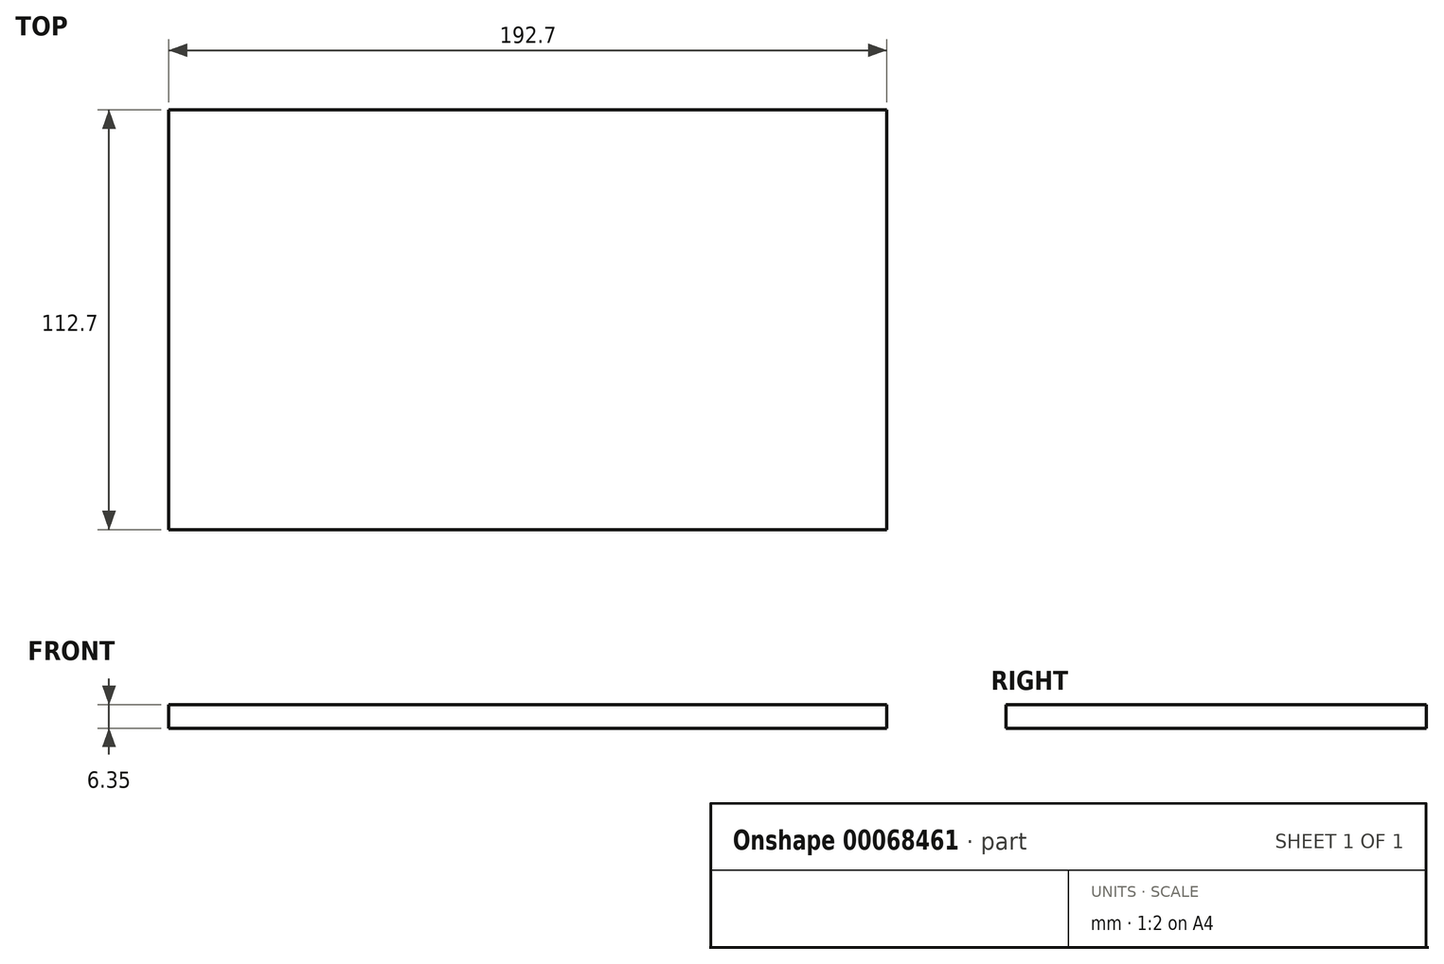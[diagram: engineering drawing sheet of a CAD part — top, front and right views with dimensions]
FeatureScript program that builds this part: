
annotation { "Feature Type Name" : "Feature", "Feature Type Description" : "" }
export const myFeature = defineFeature(function(context is Context, id is Id, definition is map)
    precondition{}
    {
        {
            var Q0;
            Q0=qCreatedBy(makeId("Top.planeOp"),FACE);
            var sketch = newSketch(context, id + "F0", { "sketchPlane" : qUnion([Q0])});
            skLineSegment(sketch, "E0.rect.bottom", {"start": v(96.35, 56.35) * mm, "end": v(-96.35, 56.35) * mm});
            skLineSegment(sketch, "E0.rect.top", {"start": v(96.35, -56.35) * mm, "end": v(-96.35, -56.35) * mm});
            skLineSegment(sketch, "E0.rect.left", {"start": v(96.35, 56.35) * mm, "end": v(96.35, -56.35) * mm});
            skLineSegment(sketch, "E0.rect.right", {"start": v(-96.35, 56.35) * mm, "end": v(-96.35, -56.35) * mm});
            skPoint(sketch, "E0.rect.middle", {"position": v(0, 0) * mm});
            skSolve(sketch);
        }
        {
            var Q0;
            Q0=makeQuery(id+"F0.imprint","IMPRINT",FACE,{"disambiguationData":[TD([[makeQuery(id+"F0.imprint","IMPRINT",EDGE,{"derivedFrom":sQuery(id+"F0.wireOp",EDGE,"E0.rect.bottom")}),1.0]])]});
            extrude(context, id + "F1", {"entities" : qUnion([Q0]), "depth" : 6.35 * mm});
        }
    });
